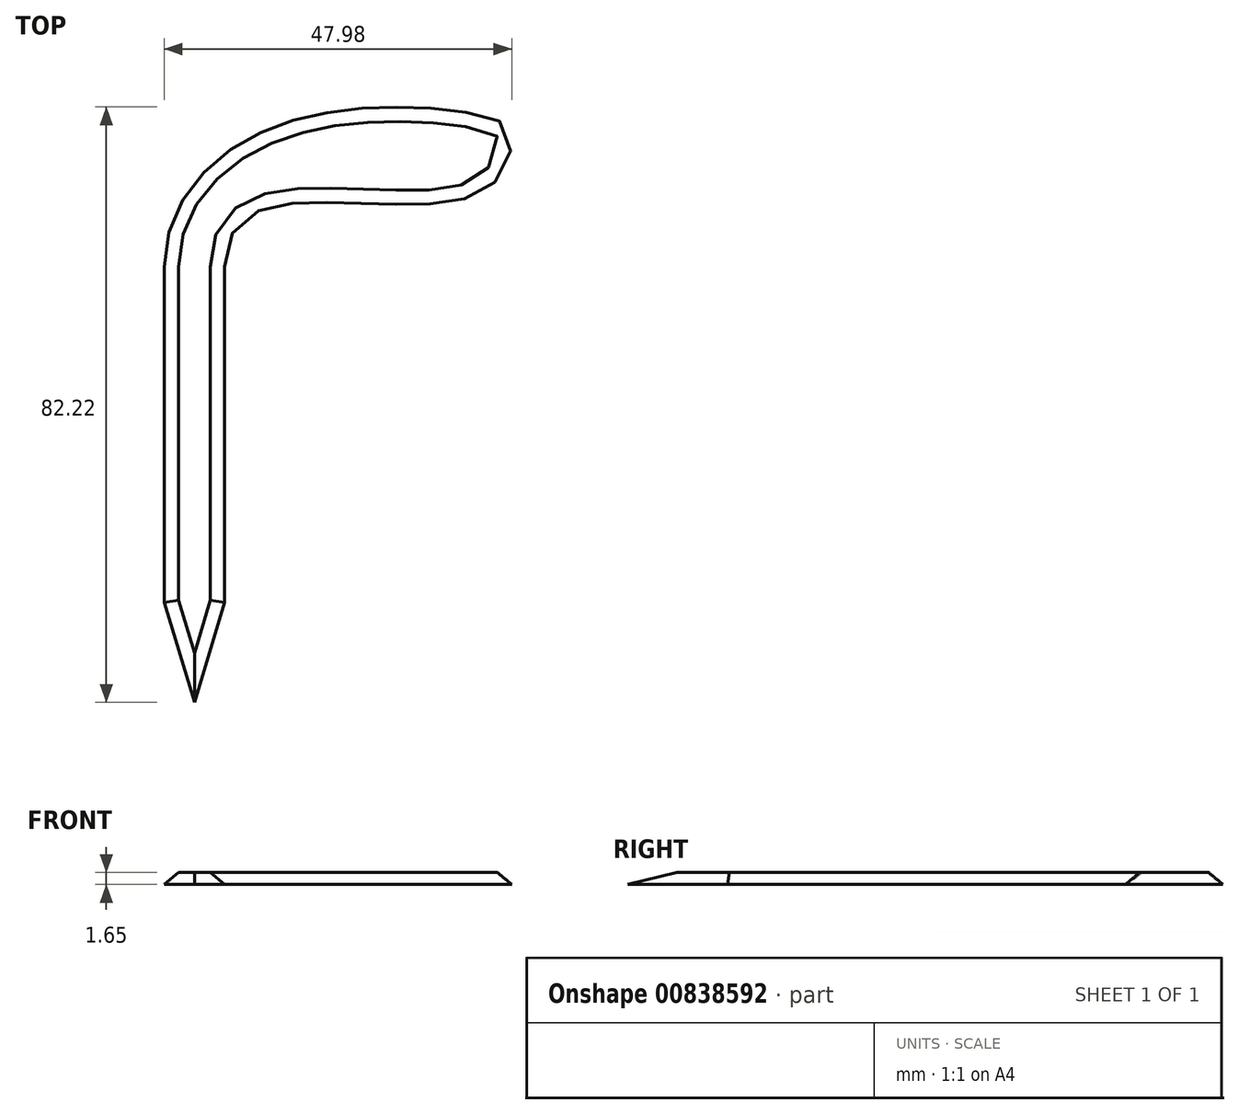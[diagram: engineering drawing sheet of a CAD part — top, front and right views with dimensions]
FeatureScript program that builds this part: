
annotation { "Feature Type Name" : "Feature", "Feature Type Description" : "" }
export const myFeature = defineFeature(function(context is Context, id is Id, definition is map)
    precondition{}
    {
        {
            var Q0;
            Q0=qCreatedBy(makeId("Top.planeOp"),FACE);
            var sketch = newSketch(context, id + "F0", { "sketchPlane" : qUnion([Q0])});
            skLineSegment(sketch, "E0", {"start": v(0, -45.96) * mm, "end": v(4.16, -32.16) * mm});
            skLineSegment(sketch, "E1", {"start": v(4.16, -32.16) * mm, "end": v(4.16, 14.2) * mm});
            skFitSpline(sketch, "E2", {"points": [v(4.16, 14.2) * mm, v(20.43, 23.05) * mm, v(40.6, 25.13) * mm, v(43.8, 32.16) * mm, v(41.33, 34.63) * mm, v(12.43, 34.05) * mm, v(-4.16, 14.2) * mm], "startDerivative": vector(0, 150.67) * mm, "endDerivative": vector(0, -129.25) * mm});
            skLineSegment(sketch, "E3", {"start": v(0, -45.96) * mm, "end": v(0, -12.71) * mm, "construction": true});
            skLineSegment(sketch, "E4.MirrorCS", {"start": v(0, -45.96) * mm, "end": v(-4.16, -32.16) * mm});
            skLineSegment(sketch, "E5.MirrorCS", {"start": v(-4.16, -32.16) * mm, "end": v(-4.16, 14.2) * mm});
            skSolve(sketch);
        }
        {
            var Q0;
            Q0=makeQuery(id+"F0.imprint","IMPRINT",FACE,{"disambiguationData":[TD([[makeQuery(id+"F0.imprint","IMPRINT",EDGE,{"derivedFrom":sQuery(id+"F0.wireOp",EDGE,"E0")}),1.0]])]});
            extrude(context, id + "F1", {"entities" : qUnion([Q0]), "depth" : 1.65 * mm, "offsetDistance" : 25.4 * mm, "hasDraft" : true, "draftAngle" : 50 * degree, "draftPullDirection" : true});
        }
    });
